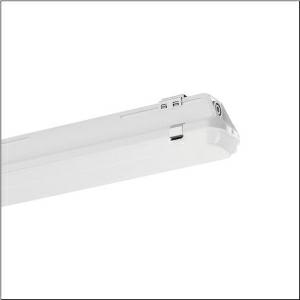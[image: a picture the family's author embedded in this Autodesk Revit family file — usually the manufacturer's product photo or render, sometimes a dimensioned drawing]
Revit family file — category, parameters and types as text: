
# Revit family: monsun_r__11_51fp109p440h_ab1f
name_source: partatom
category: Lighting Fixtures
units: mm (PartAtom-declared; Revit-internal decimal feet)

## family parameters
Cut with Voids When Loaded = No
Host = Face
Light Source = No
Part Type = Normal
Room Calculation Point = No
Round Connector Dimension = Use Diameter
Shared = No

## types (1)
- Monsun® 11 (1 x LED, 4120 lm, 22.9 W, 4000K)
    Apparent Load = 23 VA
    CIE Flux Codes = 47 77 93 94 100
    Color Rendering = 80
    Color Temperature = 4000K
    Default Elevation = 1800 mm
    Description = Monsun® 11, damp-proof luminaire, chain hanger, primary optical cover: enclosure, of PMMA, light emission: direct distribution, primary light characteristic: symmetric, installation type: suspended mounting, surface-mounted, horizontal mounting, vertical mounting, LED, rated luminous flux: 4.120lm, luminous efficacy: 180lm/W, light colour: 840, colour temperature: 4000K, control gear: ON/OFF, CLOi, with terminal, 3-pole, max. 2.5mm², mains connection: 220..240V, AC, 50/60Hz, start of lifetime: 23W, end of service life: 25W, luminaire housing, of glass-fibre reinforced polyester, uncoated, bright grey, incl. chain hanger, length: 1.590mm, width: 90mm, height: 88mm, clip for enclosure, of stainless steel (V2A), ceiling mounting element, of stainless steel (V2A), chain hanger, of stainless steel (V2A), protection rating (complete): IP66, insulation class (complete): insulation class I (protective earthing), certification: CE, ENEC, VDE, UKCA, protection symbol: D, impact resistance: IK04, permissible operating ambient temperature: -35..+40°C, standard: EN 50419, EN 60598-2-1, no direct snow, no direct sun, no direct rain, for indoor or canopied outdoor use, corresponds to IFS (International Featured Standards) requirements for safety and quality in the food industry, contact your sales advisor before using the luminaires in applications with unclear chemical exposure, large temperature fluctuations or condensation-forming humidity, LABS conformity tested according to VDMA 24364:2018-05, packaging unit: 1 piece
    Height = 89 mm
    Lamp = 1 x LED
    Lamp Light Flux = 4120 lm
    Lamp Power = 22.9 W
    Lamp count = 1
    Length = 1590 mm
    Luminous efficacy = 180 lm/W
    Manufacturer = Siteco
    ModVariant = No
    Model = 51FP109P440H
    Mounting Place = Ceiling
    Mounting Type = Surface mounted
    Number of Poles = 1
    OnlyDefault = Yes
    Power Factor = 1
    Product Name = Monsun® 11
    Product group = damp-proof luminaire
    ProductGroupID = 300
    Protection Class = Protection class I
    Protection Degree = IP 66
    RLX_Detail_Level = 1
    RLX_Emergency_Light_Flux = 0 lm
    RLX_Emergency_Type = 0
    RLX_Emergency_Type_DB = No
    RlxData = <blob elided: 88661 chars, md5=56c7022f>
    Socket = socket
    Standby Power = 0 W
    System Light Flux = 4120 lm
    System Power = 23 W
    Type Comments = Product without accessories
    Type Image = l_1349237.jpg
    URL = http://relux.com
    VarID = ---
    Voltage = 0 V
    Weight = 0.00 kg
    Width = 90 mm

## geometry (parser evidence)
native form markers: Blend x4, Sweep x13
no freeform markers — native parametric forms only
